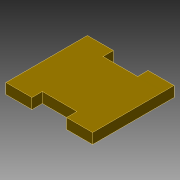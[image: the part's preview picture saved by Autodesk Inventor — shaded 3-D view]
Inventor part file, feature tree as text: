
AUTODESK INVENTOR PART (.ipt)
format: ipt  version: 2021.3 (Build 253353000, 353)  size: 105,472 bytes
history: native  units: mm
features: other x1, extrude x1, sketch x1
ambient origin geometry x8: Origin, YZ Plane, XZ Plane, XY Plane, X Axis, Y Axis, Z Axis, Center Point
bodies: Body1 (feature_tree)
feature tree (3):
  other  "Твердое тело1"
  extrude  "Выдавливание1"  Depth=50.0mm
  sketch  "Эскиз1"
